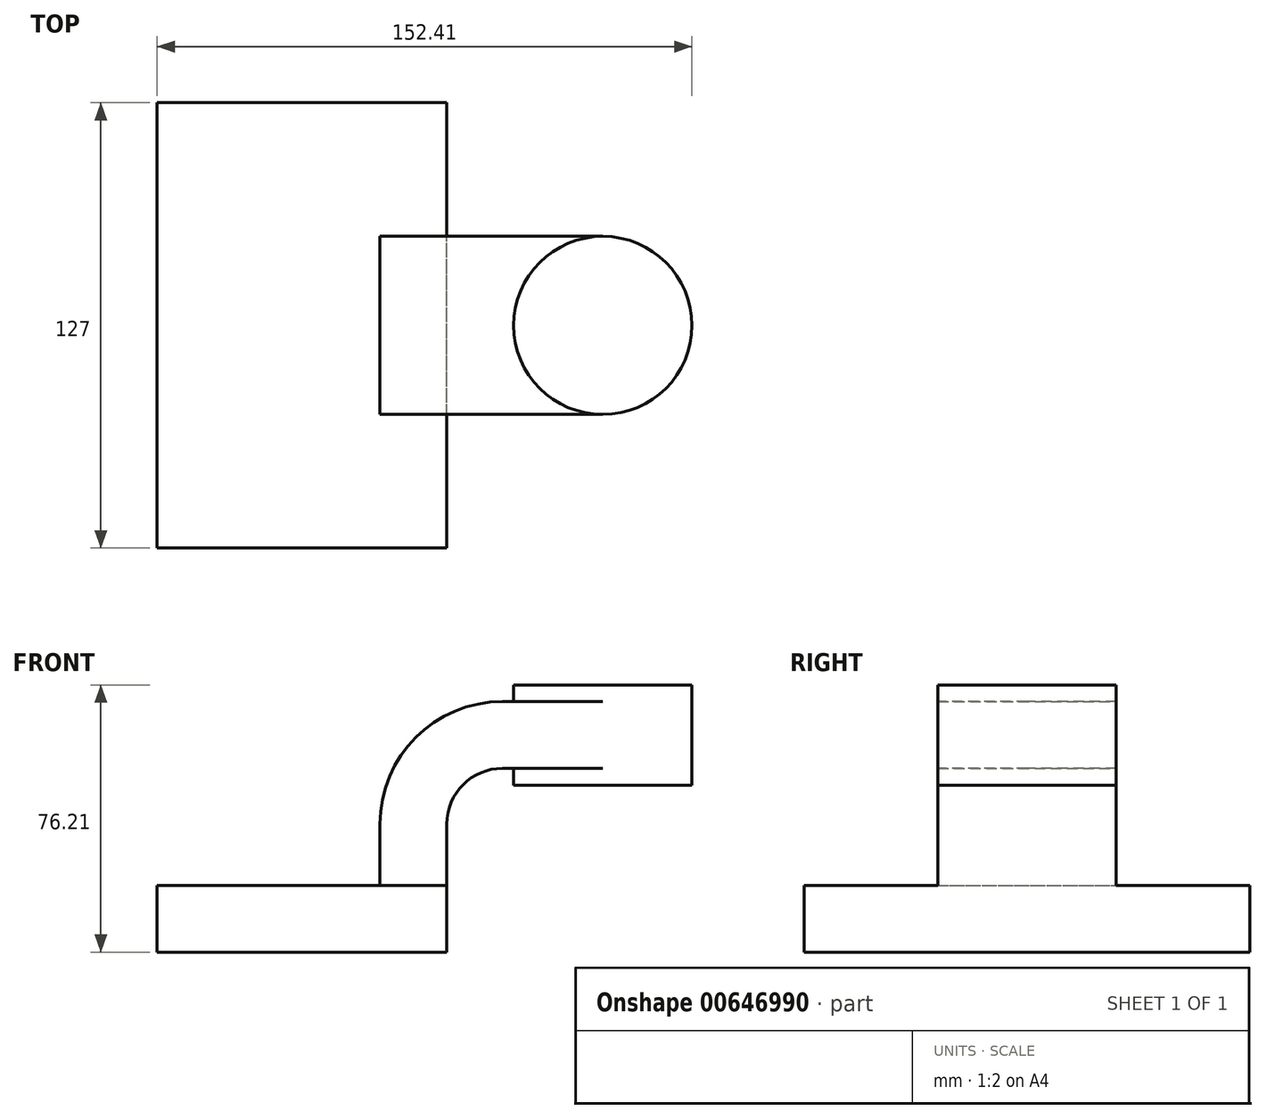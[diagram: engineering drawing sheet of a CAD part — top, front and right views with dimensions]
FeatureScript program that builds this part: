
annotation { "Feature Type Name" : "Feature", "Feature Type Description" : "" }
export const myFeature = defineFeature(function(context is Context, id is Id, definition is map)
    precondition{}
    {
        {
            var Q0;
            Q0=qCreatedBy(makeId("Front.planeOp"),FACE);
            var sketch = newSketch(context, id + "F0", { "sketchPlane" : qUnion([Q0])});
            skLineSegment(sketch, "E0.bottom", {"start": v(41.27, 9.53) * mm, "end": v(-41.28, 9.52) * mm});
            skLineSegment(sketch, "E0.top", {"start": v(41.28, -9.52) * mm, "end": v(-41.28, -9.53) * mm});
            skLineSegment(sketch, "E0.left", {"start": v(41.27, 9.53) * mm, "end": v(41.28, -9.52) * mm});
            skLineSegment(sketch, "E0.right", {"start": v(-41.28, 9.52) * mm, "end": v(-41.28, -9.53) * mm});
            skPoint(sketch, "E0.middle", {"position": v(0, 0) * mm});
            skLineSegment(sketch, "E1.bottom", {"start": v(111.13, 38.1) * mm, "end": v(60.32, 38.1) * mm});
            skLineSegment(sketch, "E1.top", {"start": v(111.12, 66.68) * mm, "end": v(60.32, 66.68) * mm});
            skLineSegment(sketch, "E1.left", {"start": v(111.13, 38.1) * mm, "end": v(111.12, 66.68) * mm});
            skLineSegment(sketch, "E1.right", {"start": v(60.32, 38.1) * mm, "end": v(60.32, 66.68) * mm});
            skPoint(sketch, "E1.middle", {"position": v(85.73, 52.39) * mm});
            skLineSegment(sketch, "E2", {"start": v(41.27, 9.53) * mm, "end": v(41.27, 27) * mm});
            skArc(sketch, "E3", {"start": v(41.28, 27) * mm, "mid": v(45.92, 38.23) * mm, "end": v(57.15, 42.88) * mm});
            skLineSegment(sketch, "E4", {"start": v(57.15, 42.88) * mm, "end": v(85.73, 42.88) * mm});
            skLineSegment(sketch, "E5.0", {"start": v(57.15, 61.93) * mm, "end": v(85.73, 61.93) * mm});
            skArc(sketch, "E5.1", {"start": v(22.23, 27) * mm, "mid": v(32.45, 51.7) * mm, "end": v(57.15, 61.93) * mm});
            skLineSegment(sketch, "E5.2", {"start": v(22.23, 9.53) * mm, "end": v(22.23, 27) * mm});
            skFitSpline(sketch, "E6", {"points": [v(-41.28, 9.52) * mm, v(57.15, 61.93) * mm], "startDerivative": vector(2.52, 126.47) * mm, "endDerivative": vector(123.98, -2.03) * mm});
            skLineSegment(sketch, "E7", {"start": v(85.72, 38.1) * mm, "end": v(85.72, 66.68) * mm});
            skSolve(sketch);
        }
        {
            var Q0;
            Q0=makeQuery(id+"F0.imprint","IMPRINT",FACE,{"disambiguationData":[TD([[makeQuery(id+"F0.imprint","IMPRINT",EDGE,{"derivedFrom":sQuery(id+"F0.wireOp",EDGE,"E0.top")}),-1.0]])]});
            extrude(context, id + "F1", {"entities" : qUnion([Q0]), "endBound" : BoundingType.SYMMETRIC, "depth" : 127 * mm, "offsetDistance" : 25.4 * mm});
        }
        {
            var Q0;
            {var subQ1=sQuery(id+"F0.wireOp",EDGE,"E2");Q0=makeQuery(id+"F0.imprint","IMPRINT",FACE,{"disambiguationData":[TD([[makeQuery(id+"F0.imprint","IMPRINT",EDGE,{"derivedFrom":subQ1}),1.0]])]});}
            extrude(context, id + "F2", {"entities" : qUnion([Q0]), "operationType" : NewBodyOperationType.ADD, "endBound" : BoundingType.SYMMETRIC, "depth" : 50.8 * mm, "offsetDistance" : 25.4 * mm});
        }
        {
            var Q0;
            Q0=makeQuery(id+"F0.imprint","IMPRINT",FACE,{"disambiguationData":[TD([[makeQuery(id+"F0.imprint","IMPRINT",EDGE,{"derivedFrom":sQuery(id+"F0.wireOp",EDGE,"E5.1")}),1.0]])]});
            extrude(context, id + "F3", {"entities" : qUnion([Q0]), "operationType" : NewBodyOperationType.ADD, "endBound" : BoundingType.SYMMETRIC, "depth" : 15.88 * mm, "offsetDistance" : 25.4 * mm});
        }
        {
            var Q0;
            {var subQ0=sQuery(id+"F0.wireOp",EDGE,"E4");var subQ1=sQuery(id+"F0.wireOp",EDGE,"E1.right");var subQ2=makeQuery(id+"F0.imprint","INTERSECT",VERTEX,{"derivedFrom":[subQ1,subQ0]});Q0=makeQuery(id+"F0.imprint","IMPRINT",FACE,{"disambiguationData":[TD([[makeQuery(id+"F0.imprint","IMPRINT",EDGE,{"disambiguationData":[TD([[subQ2,-1.0]])],"derivedFrom":subQ1}),-1.0]])]});}
            extrude(context, id + "F4", {"entities" : qUnion([Q0]), "operationType" : NewBodyOperationType.ADD, "endBound" : BoundingType.SYMMETRIC, "depth" : 50.8 * mm, "offsetDistance" : 25.4 * mm});
        }
        {
            var Q0;
            {var subQ0=sQuery(id+"F0.wireOp",EDGE,"E1.left");Q0=makeQuery(id+"F0.imprint","IMPRINT",FACE,{"disambiguationData":[TD([[makeQuery(id+"F0.imprint","IMPRINT",EDGE,{"derivedFrom":subQ0}),1.0]])]});}
            var Q1;
            Q1=sQuery(id+"F0.wireOp",EDGE,"E7");
            revolve(context, id + "F5", {"operationType" : NewBodyOperationType.ADD, "entities" : qUnion([Q0]), "axis" : qUnion([Q1]), "revolveType" : RevolveType.FULL});
        }
    });
